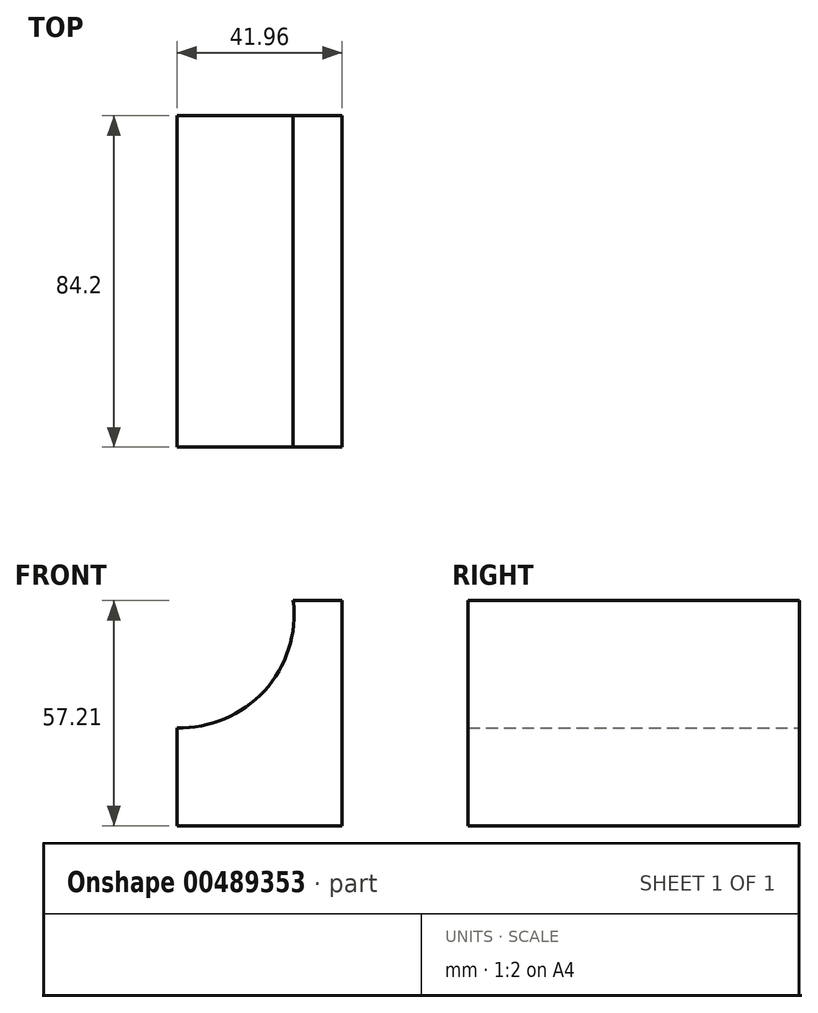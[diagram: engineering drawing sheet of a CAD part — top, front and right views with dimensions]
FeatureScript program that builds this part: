
annotation { "Feature Type Name" : "Feature", "Feature Type Description" : "" }
export const myFeature = defineFeature(function(context is Context, id is Id, definition is map)
    precondition{}
    {
        {
            var Q0;
            Q0=qCreatedBy(makeId("Front.planeOp"),FACE);
            var sketch = newSketch(context, id + "F0", { "sketchPlane" : qUnion([Q0])});
            skLineSegment(sketch, "E0", {"start": v(0, 0) * mm, "end": v(0, 57.21) * mm});
            skLineSegment(sketch, "E1", {"start": v(-12.4, 57.21) * mm, "end": v(0, 57.21) * mm});
            skLineSegment(sketch, "E2", {"start": v(0, 0) * mm, "end": v(-41.96, 0) * mm});
            skLineSegment(sketch, "E3", {"start": v(-41.96, 0) * mm, "end": v(-41.96, 24.9) * mm});
            skArc(sketch, "E4", {"start": v(-41.96, 24.9) * mm, "mid": v(-19.74, 34.26) * mm, "end": v(-12.4, 57.21) * mm});
            skSolve(sketch);
        }
        {
            var Q0;
            Q0 = qSketchRegion(id + "F0", true);
            extrude(context, id + "F1", {"entities" : qUnion([Q0]), "endBound" : BoundingType.SYMMETRIC, "depth" : 84.2 * mm, "offsetDistance" : 25 * mm});
        }
    });
